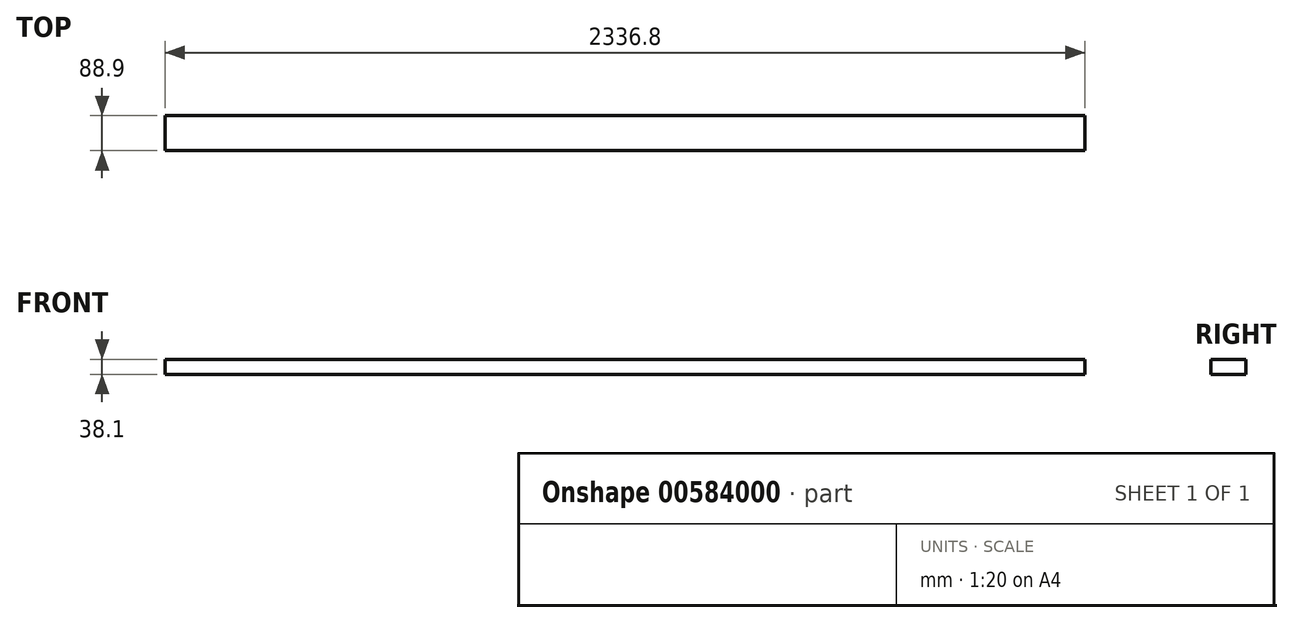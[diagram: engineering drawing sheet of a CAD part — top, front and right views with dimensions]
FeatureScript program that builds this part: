
annotation { "Feature Type Name" : "Feature", "Feature Type Description" : "" }
export const myFeature = defineFeature(function(context is Context, id is Id, definition is map)
    precondition{}
    {
        {
            var Q0;
            Q0=qCreatedBy(makeId("Top.planeOp"),FACE);
            var sketch = newSketch(context, id + "F0", { "sketchPlane" : qUnion([Q0])});
            skLineSegment(sketch, "E0.bottom", {"start": v(-604.36, 0) * mm, "end": v(1732.44, 0) * mm});
            skLineSegment(sketch, "E0.top", {"start": v(-604.36, 88.9) * mm, "end": v(1732.44, 88.9) * mm});
            skLineSegment(sketch, "E0.left", {"start": v(-604.36, 0) * mm, "end": v(-604.36, 88.9) * mm});
            skLineSegment(sketch, "E0.right", {"start": v(1732.44, 0) * mm, "end": v(1732.44, 88.9) * mm});
            skSolve(sketch);
        }
        {
            var Q0;
            Q0=makeQuery(id+"F0.imprint","IMPRINT",FACE,{"disambiguationData":[TD([[makeQuery(id+"F0.imprint","IMPRINT",EDGE,{"derivedFrom":sQuery(id+"F0.wireOp",EDGE,"E0.bottom")}),1.0]])]});
            extrude(context, id + "F1", {"entities" : qUnion([Q0]), "depth" : 38.1 * mm, "offsetDistance" : 25.4 * mm});
        }
    });
